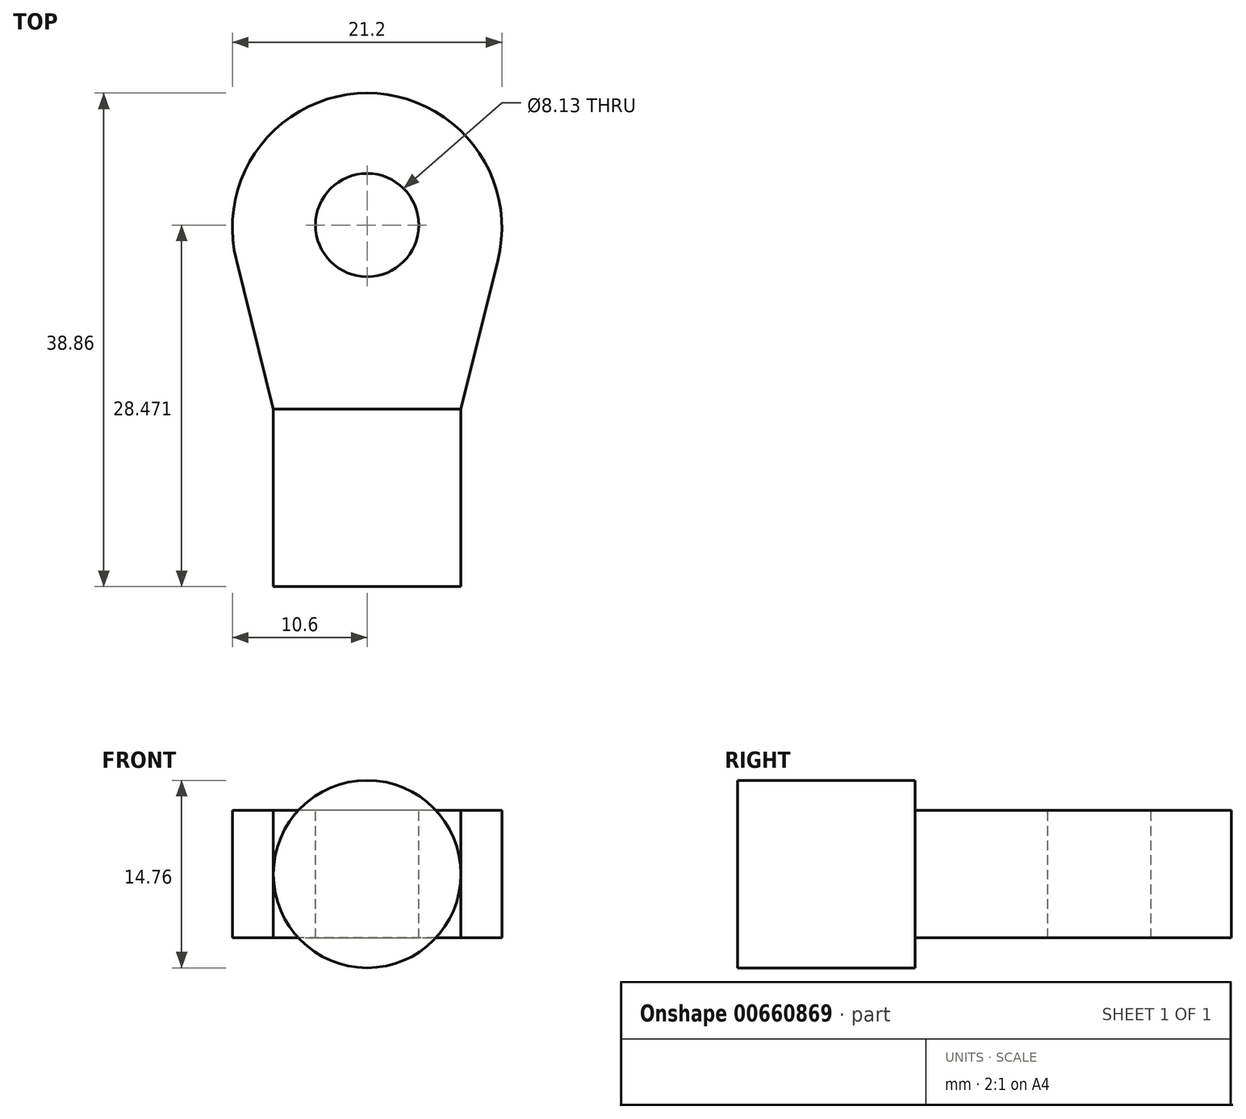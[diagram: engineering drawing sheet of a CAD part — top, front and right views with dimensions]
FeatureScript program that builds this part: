
annotation { "Feature Type Name" : "Feature", "Feature Type Description" : "" }
export const myFeature = defineFeature(function(context is Context, id is Id, definition is map)
    precondition{}
    {
        {
            var Q0;
            Q0=qCreatedBy(makeId("Front.planeOp"),FACE);
            var sketch = newSketch(context, id + "F0", { "sketchPlane" : qUnion([Q0])});
            skCircle(sketch, "E0", {"center": v(0, 0) * mm, "radius": 12.7 * mm});
            skSolve(sketch);
        }
        {
            var Q0;
            Q0=makeQuery(id+"F0.imprint","IMPRINT",FACE,{"disambiguationData":[TD([[makeQuery(id+"F0.imprint","IMPRINT",EDGE,{"derivedFrom":sQuery(id+"F0.wireOp",EDGE,"E0")}),1.0]])]});
            extrude(context, id + "F1", {"entities" : qUnion([Q0]), "depth" : 38.86 * mm, "offsetDistance" : 25.4 * mm});
        }
        {
            var Q0;
            Q0=makeQuery(id+"F1.opExtrude","CAP_FACE",FACE,{"disambiguationData":[OSD([sQuery(id+"F0.wireOp",EDGE,"E0")])],"isStart":false});
            var sketch = newSketch(context, id + "F2", { "sketchPlane" : qUnion([Q0])});
            skCircle(sketch, "E1", {"center": v(0, 0) * mm, "radius": 7.38 * mm});
            skSolve(sketch);
        }
        {
            var Q0;
            Q0=makeQuery(id+"F2.imprint","IMPRINT",FACE,{"disambiguationData":[TD([[makeQuery(id+"F2.imprint","IMPRINT",EDGE,{"derivedFrom":sQuery(id+"F2.wireOp",EDGE,"E1")}),-1.0]])]});
            extrude(context, id + "F3", {"entities" : qUnion([Q0]), "operationType" : NewBodyOperationType.REMOVE, "oppositeDirection" : true, "depth" : 13.97 * mm, "offsetDistance" : 25.4 * mm});
        }
        {
            var Q0;
            Q0=makeQuery(id+"F1.opExtrude","CAP_FACE",FACE,{"disambiguationData":[OSD([sQuery(id+"F0.wireOp",EDGE,"E0")])],"isStart":true});
            var sketch = newSketch(context, id + "F4", { "sketchPlane" : qUnion([Q0])});
            skLineSegment(sketch, "E2", {"start": v(-11.67, 5.02) * mm, "end": v(11.67, 5.02) * mm});
            skLineSegment(sketch, "E3", {"start": v(-11.67, -5.02) * mm, "end": v(11.67, -5.02) * mm});
            skCircle(sketch, "E4.0", {"center": v(0, 0) * mm, "radius": 12.7 * mm});
            skSolve(sketch);
        }
        {
            var Q0;
            {var subQ0=sQuery(id+"F4.wireOp",EDGE,"E2");Q0=makeQuery(id+"F4.imprint","IMPRINT",FACE,{"disambiguationData":[TD([[makeQuery(id+"F4.imprint","IMPRINT",EDGE,{"derivedFrom":subQ0}),1.0]])]});}
            var Q1;
            {var subQ0=sQuery(id+"F4.wireOp",EDGE,"E3");Q1=makeQuery(id+"F4.imprint","IMPRINT",FACE,{"disambiguationData":[TD([[makeQuery(id+"F4.imprint","IMPRINT",EDGE,{"derivedFrom":subQ0}),-1.0]])]});}
            extrude(context, id + "F5", {"entities" : qUnion([Q0, Q1]), "operationType" : NewBodyOperationType.REMOVE, "oppositeDirection" : true, "depth" : 24.9 * mm, "offsetDistance" : 25.4 * mm});
        }
        {
            var Q0;
            Q0=makeQuery(id+"F5.boolean.opBoolean","COPY",FACE,{"derivedFrom":makeQuery(id+"F5.opExtrude","SWEPT_FACE",FACE,{"disambiguationData":[OSD([sQuery(id+"F4.wireOp",EDGE,"E2")])]})});
            var sketch = newSketch(context, id + "F6", { "sketchPlane" : qUnion([Q0])});
            skLineSegment(sketch, "E5", {"start": v(-12.7, -24.9) * mm, "end": v(-12.7, 0) * mm});
            skLineSegment(sketch, "E6", {"start": v(12.7, 0) * mm, "end": v(12.7, -24.9) * mm});
            skLineSegment(sketch, "E7", {"start": v(-7.38, -38.86) * mm, "end": v(-7.38, -24.9) * mm});
            skLineSegment(sketch, "E8", {"start": v(7.38, -24.9) * mm, "end": v(7.38, -38.86) * mm});
            skCircle(sketch, "E9", {"center": v(0, -10.39) * mm, "radius": 4.06 * mm});
            skCircle(sketch, "E10", {"center": v(0, -10.6) * mm, "radius": 10.6 * mm});
            skLineSegment(sketch, "E11", {"start": v(-7.38, -24.9) * mm, "end": v(-10.3, -13.16) * mm});
            skLineSegment(sketch, "E12", {"start": v(7.38, -24.9) * mm, "end": v(10.3, -13.16) * mm});
            skLineSegment(sketch, "E13", {"start": v(0, 0) * mm, "end": v(-12.7, 0) * mm});
            skLineSegment(sketch, "E14", {"start": v(-12.7, -24.9) * mm, "end": v(-7.38, -24.9) * mm});
            skLineSegment(sketch, "E15", {"start": v(0, 0) * mm, "end": v(12.7, 0) * mm});
            skLineSegment(sketch, "E16", {"start": v(12.7, -24.9) * mm, "end": v(7.38, -24.9) * mm});
            skSolve(sketch);
        }
        {
            var Q0;
            {var subQ4=sQuery(id+"F6.wireOp",EDGE,"E11");Q0=makeQuery(id+"F6.imprint","IMPRINT",FACE,{"disambiguationData":[TD([[makeQuery(id+"F6.imprint","IMPRINT",EDGE,{"derivedFrom":subQ4}),1.0]])]});}
            var Q1;
            {var subQ0=sQuery(id+"F6.wireOp",EDGE,"E5");Q1=makeQuery(id+"F6.imprint","IMPRINT",FACE,{"disambiguationData":[TD([[makeQuery(id+"F6.imprint","IMPRINT",EDGE,{"derivedFrom":subQ0}),-1.0]])]});}
            var Q2;
            {var subQ4=sQuery(id+"F6.wireOp",EDGE,"E12");Q2=makeQuery(id+"F6.imprint","IMPRINT",FACE,{"disambiguationData":[TD([[makeQuery(id+"F6.imprint","IMPRINT",EDGE,{"derivedFrom":subQ4}),-1.0]])]});}
            var Q3;
            {var subQ0=sQuery(id+"F6.wireOp",EDGE,"E6");Q3=makeQuery(id+"F6.imprint","IMPRINT",FACE,{"disambiguationData":[TD([[makeQuery(id+"F6.imprint","IMPRINT",EDGE,{"derivedFrom":subQ0}),-1.0]])]});}
            var Q4;
            Q4=makeQuery(id+"F6.imprint","IMPRINT",FACE,{"disambiguationData":[TD([[makeQuery(id+"F6.imprint","IMPRINT",EDGE,{"derivedFrom":sQuery(id+"F6.wireOp",EDGE,"E9")}),1.0]])]});
            extrude(context, id + "F7", {"entities" : qUnion([Q0, Q1, Q2, Q3, Q4]), "operationType" : NewBodyOperationType.REMOVE, "oppositeDirection" : true, "depth" : 25.4 * mm, "offsetDistance" : 25.4 * mm});
        }
    });
